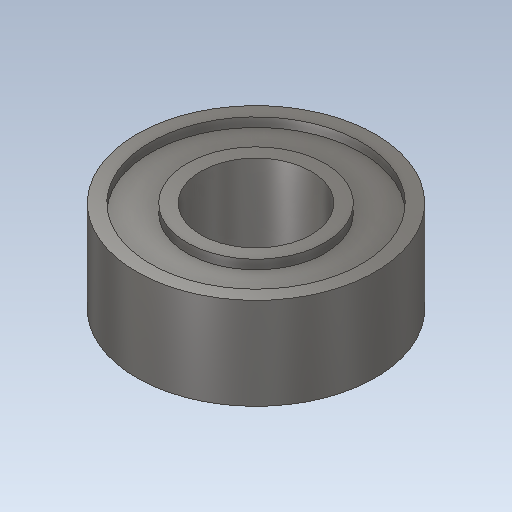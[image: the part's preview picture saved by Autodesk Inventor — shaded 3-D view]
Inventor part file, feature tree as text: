
AUTODESK INVENTOR PART (.ipt)
format: ipt  version: 2020 (Build 240168000, 168)  size: 159,744 bytes
history: native  units: mm
features: extrude x3, sketch x3, projected_geometry x2
ambient origin geometry x8: Origin, YZ Plane, XZ Plane, XY Plane, X Axis, Y Axis, Z Axis, Center Point
bodies: 实体1 (feature_tree)
feature tree (8):
  extrude  "拉伸1"  Depth=6.0mm
  extrude  "拉伸2"  Depth=5.0mm
  extrude  "拉伸3"  Depth=0.5mm TaperAngle=0.0deg
  sketch  "草图1"  dims[d0=13.0mm d1=6.0mm]
  sketch  "草图2"  dims[d2=5.0mm d3=0.0mm d4=11.5mm]
  projected_geometry  "投影回路1"
  sketch  "草图3"  dims[d5=7.5mm d6=0.5mm d7=0.0mm d8=0.5mm d9=0.0mm]
  projected_geometry  "投影回路2"
